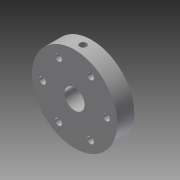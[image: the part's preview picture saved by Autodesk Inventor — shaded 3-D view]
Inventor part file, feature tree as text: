
AUTODESK INVENTOR PART (.ipt)
format: ipt  version: 2015 (Build 190159000, 159)  size: 134,656 bytes
history: native  units: mm
features: sketch x3, extrude x2, other x1, revolve x1
ambient origin geometry x8: Origin, YZ Plane, XZ Plane, XY Plane, X Axis, Y Axis, Z Axis, Center Point
bodies: Body1 (feature_tree)
feature tree (7):
  other  "Sólido1"
  sketch  "Boceto1"  dims[d4=90.0deg d5=111.0mm d6=0.0mm]
  revolve  "Revolución1"  [1 undecoded]
  extrude  "Extrusión1"  Depth=2.0mm
  extrude  "Extrusión2"  Depth=2.0mm
  sketch  "Boceto3"  dims[d10=2.0mm d11=2.0mm d12=2.0mm d13=2.0mm d14=12.0mm d15=0.0mm]
  sketch  "Boceto2"  dims[d8=2.0mm d9=2.0mm]
note: 1 required parameter value undecoded (feature->parameter linkage not recoverable at this tier; creation-order binding heuristic only, values carry confidence <= 0.55)
